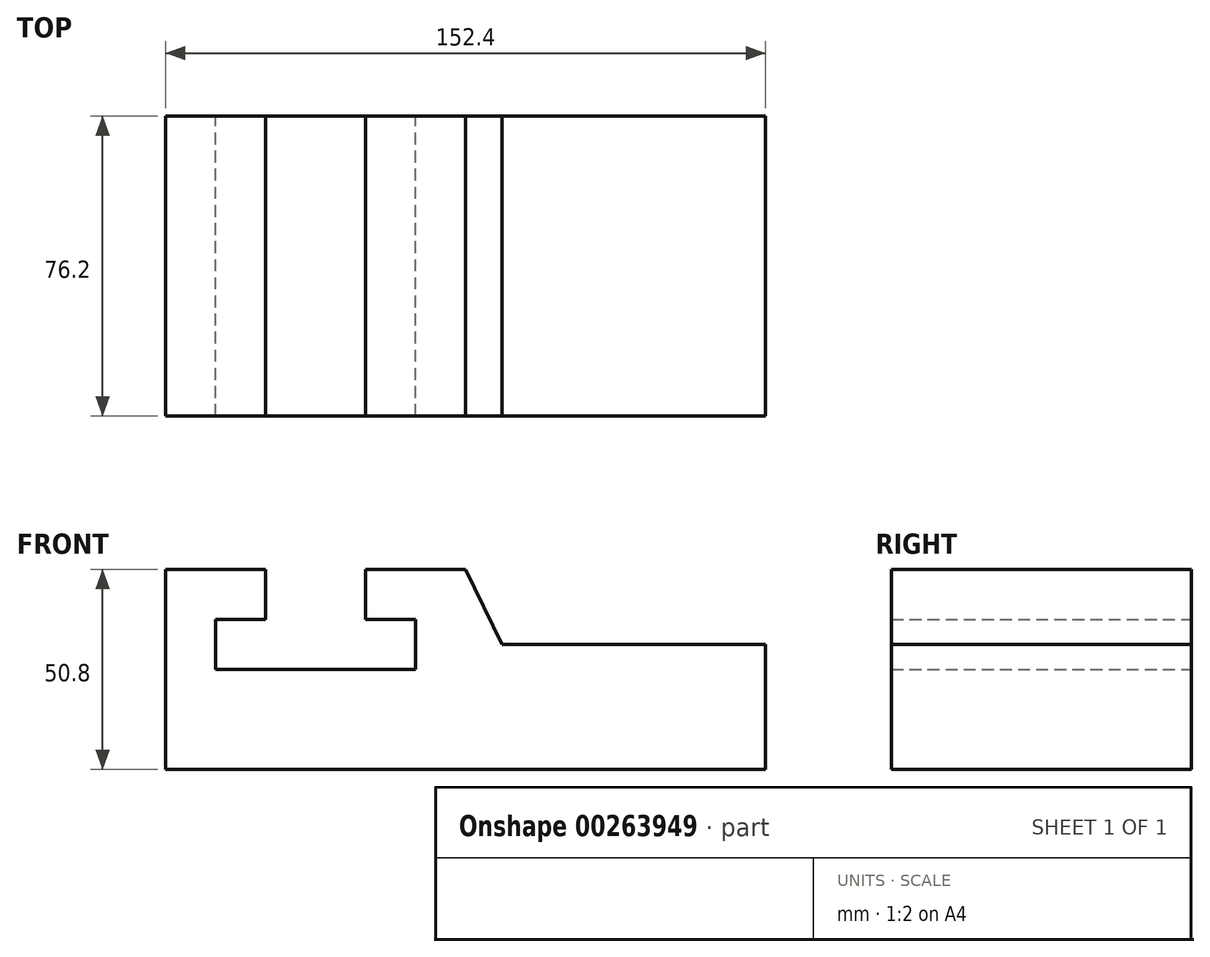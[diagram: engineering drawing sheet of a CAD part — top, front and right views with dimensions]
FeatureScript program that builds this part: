
annotation { "Feature Type Name" : "Feature", "Feature Type Description" : "" }
export const myFeature = defineFeature(function(context is Context, id is Id, definition is map)
    precondition{}
    {
        {
            var Q0;
            Q0=qCreatedBy(makeId("Front.planeOp"),FACE);
            var sketch = newSketch(context, id + "F0", { "sketchPlane" : qUnion([Q0])});
            skLineSegment(sketch, "E0", {"start": v(-76.2, 0) * mm, "end": v(-63.5, 0) * mm});
            skLineSegment(sketch, "E1", {"start": v(-76.2, 0) * mm, "end": v(-76.2, 25.4) * mm});
            skLineSegment(sketch, "E2", {"start": v(-76.2, 25.4) * mm, "end": v(-76.2, 50.8) * mm});
            skLineSegment(sketch, "E3", {"start": v(-76.2, 50.8) * mm, "end": v(-50.8, 50.8) * mm});
            skLineSegment(sketch, "E4", {"start": v(-50.8, 50.8) * mm, "end": v(-50.8, 38.1) * mm});
            skLineSegment(sketch, "E5", {"start": v(-50.8, 38.1) * mm, "end": v(-63.5, 38.1) * mm});
            skLineSegment(sketch, "E6", {"start": v(-63.5, 38.1) * mm, "end": v(-63.5, 25.4) * mm});
            skLineSegment(sketch, "E7", {"start": v(-63.5, 25.4) * mm, "end": v(-12.7, 25.4) * mm});
            skLineSegment(sketch, "E8", {"start": v(-12.7, 25.4) * mm, "end": v(-12.7, 38.1) * mm});
            skLineSegment(sketch, "E9", {"start": v(-12.7, 38.1) * mm, "end": v(-25.4, 38.1) * mm});
            skLineSegment(sketch, "E10", {"start": v(-25.4, 38.1) * mm, "end": v(-25.4, 50.8) * mm});
            skLineSegment(sketch, "E11", {"start": v(-25.4, 50.8) * mm, "end": v(0, 50.8) * mm});
            skLineSegment(sketch, "E12", {"start": v(0, 50.8) * mm, "end": v(6.35, 50.8) * mm, "construction": true});
            skLineSegment(sketch, "E13", {"start": v(6.35, 50.8) * mm, "end": v(6.35, 38.1) * mm, "construction": true});
            skLineSegment(sketch, "E14", {"start": v(-63.5, 0) * mm, "end": v(76.2, 0) * mm});
            skLineSegment(sketch, "E15", {"start": v(76.2, 0) * mm, "end": v(76.2, 25.4) * mm});
            skLineSegment(sketch, "E16", {"start": v(76.2, 25.4) * mm, "end": v(76.2, 31.75) * mm});
            skLineSegment(sketch, "E17", {"start": v(76.2, 31.75) * mm, "end": v(9.2, 31.75) * mm});
            skLineSegment(sketch, "E18", {"start": v(9.2, 31.75) * mm, "end": v(0, 50.8) * mm});
            skSolve(sketch);
        }
        {
            var Q0;
            Q0=makeQuery(id+"F0.imprint","IMPRINT",FACE,{"disambiguationData":[TD([[makeQuery(id+"F0.imprint","IMPRINT",EDGE,{"derivedFrom":sQuery(id+"F0.wireOp",EDGE,"E0")}),1.0]])]});
            extrude(context, id + "F1", {"entities" : qUnion([Q0]), "depth" : 76.2 * mm});
        }
    });
